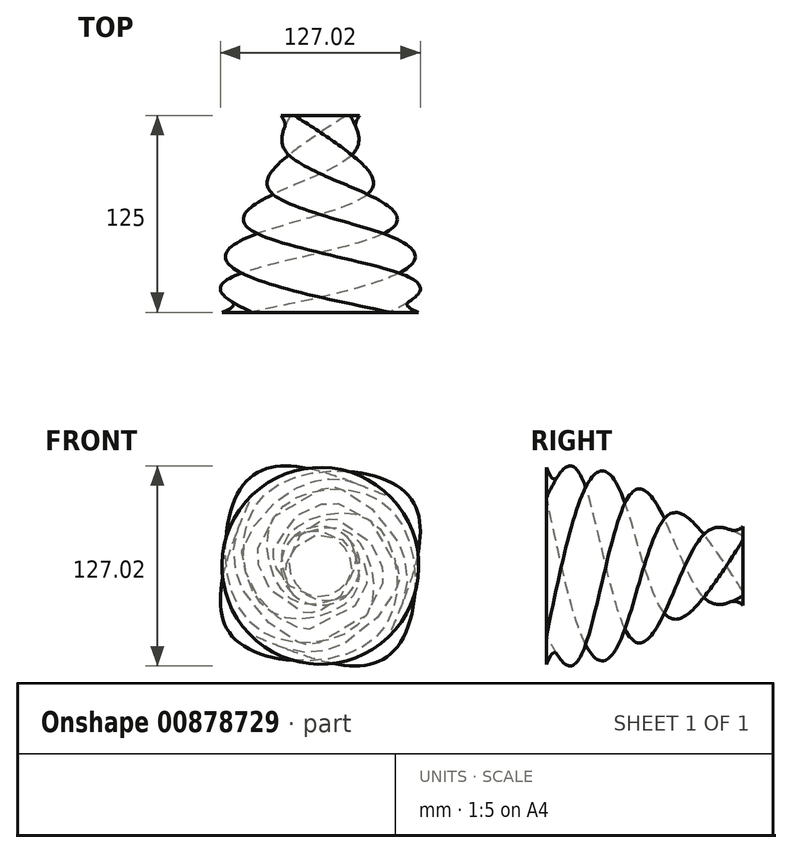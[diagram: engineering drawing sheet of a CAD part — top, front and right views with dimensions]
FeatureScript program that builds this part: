
annotation { "Feature Type Name" : "Feature", "Feature Type Description" : "" }
export const myFeature = defineFeature(function(context is Context, id is Id, definition is map)
    precondition{}
    {
        {
            var Q0;
            Q0=qCreatedBy(makeId("Front.planeOp"),FACE);
            cPlane(context, id + "F0", {"entities" : qUnion([Q0]), "cplaneType" : CPlaneType.OFFSET, "offset" : 25 * mm, "width" : 150 * mm, "height" : 150 * mm});
        }
        {
            var Q0;
            Q0=qCreatedBy(id+"F0.planeOp",FACE);
            cPlane(context, id + "F1", {"entities" : qUnion([Q0]), "cplaneType" : CPlaneType.OFFSET, "offset" : 25 * mm, "width" : 150 * mm, "height" : 150 * mm});
        }
        {
            var Q0;
            Q0=qCreatedBy(id+"F1.planeOp",FACE);
            cPlane(context, id + "F2", {"entities" : qUnion([Q0]), "cplaneType" : CPlaneType.OFFSET, "offset" : 25 * mm, "width" : 150 * mm, "height" : 150 * mm});
        }
        {
            var Q0;
            Q0=qCreatedBy(id+"F2.planeOp",FACE);
            cPlane(context, id + "F3", {"entities" : qUnion([Q0]), "cplaneType" : CPlaneType.OFFSET, "offset" : 25 * mm, "width" : 150 * mm, "height" : 150 * mm});
        }
        {
            var Q0;
            Q0=qCreatedBy(id+"F3.planeOp",FACE);
            cPlane(context, id + "F4", {"entities" : qUnion([Q0]), "cplaneType" : CPlaneType.OFFSET, "offset" : 25 * mm, "width" : 150 * mm, "height" : 150 * mm});
        }
        {
            var Q0;
            Q0=qCreatedBy(makeId("Front.planeOp"),FACE);
            var sketch = newSketch(context, id + "F5", { "sketchPlane" : qUnion([Q0])});
            skCircle(sketch, "E0", {"center": v(0, 0) * mm, "radius": 25 * mm});
            skPoint(sketch, "E1", {"position": v(-16.54, 18.75) * mm});
            skPoint(sketch, "E2", {"position": v(16.54, 18.75) * mm});
            skPoint(sketch, "E3", {"position": v(20.2, -14.74) * mm});
            skPoint(sketch, "E4", {"position": v(-18.95, -16.3) * mm});
            skSolve(sketch);
        }
        {
            var Q0;
            Q0=qCreatedBy(id+"F0.planeOp",FACE);
            var sketch = newSketch(context, id + "F6", { "sketchPlane" : qUnion([Q0])});
            skLineSegment(sketch, "E5.bottom", {"start": v(20, 20) * mm, "end": v(-20, 20) * mm});
            skLineSegment(sketch, "E5.top", {"start": v(20, -20) * mm, "end": v(-20, -20) * mm});
            skLineSegment(sketch, "E5.left", {"start": v(20, 20) * mm, "end": v(20, -20) * mm});
            skLineSegment(sketch, "E5.right", {"start": v(-20, 20) * mm, "end": v(-20, -20) * mm});
            skPoint(sketch, "E5.middle", {"position": v(0, 0) * mm});
            skSolve(sketch);
        }
        {
            var Q0;
            Q0=qCreatedBy(id+"F1.planeOp",FACE);
            var sketch = newSketch(context, id + "F7", { "sketchPlane" : qUnion([Q0])});
            skLineSegment(sketch, "E6.bottom", {"start": v(30, 30) * mm, "end": v(-30, 30) * mm});
            skLineSegment(sketch, "E6.top", {"start": v(30, -30) * mm, "end": v(-30, -30) * mm});
            skLineSegment(sketch, "E6.left", {"start": v(30, 30) * mm, "end": v(30, -30) * mm});
            skLineSegment(sketch, "E6.right", {"start": v(-30, 30) * mm, "end": v(-30, -30) * mm});
            skPoint(sketch, "E6.middle", {"position": v(0, 0) * mm});
            skSolve(sketch);
        }
        {
            var Q0;
            Q0=qCreatedBy(id+"F2.planeOp",FACE);
            var sketch = newSketch(context, id + "F8", { "sketchPlane" : qUnion([Q0])});
            skLineSegment(sketch, "E7.bottom", {"start": v(40, 40) * mm, "end": v(-40, 40) * mm});
            skLineSegment(sketch, "E7.top", {"start": v(40, -40) * mm, "end": v(-40, -40) * mm});
            skLineSegment(sketch, "E7.left", {"start": v(40, 40) * mm, "end": v(40, -40) * mm});
            skLineSegment(sketch, "E7.right", {"start": v(-40, 40) * mm, "end": v(-40, -40) * mm});
            skPoint(sketch, "E7.middle", {"position": v(0, 0) * mm});
            skSolve(sketch);
        }
        {
            var Q0;
            Q0=qCreatedBy(id+"F3.planeOp",FACE);
            var sketch = newSketch(context, id + "F9", { "sketchPlane" : qUnion([Q0])});
            skLineSegment(sketch, "E8.bottom", {"start": v(50, 50) * mm, "end": v(-50, 50) * mm});
            skLineSegment(sketch, "E8.top", {"start": v(50, -50) * mm, "end": v(-50, -50) * mm});
            skLineSegment(sketch, "E8.left", {"start": v(50, 50) * mm, "end": v(50, -50) * mm});
            skLineSegment(sketch, "E8.right", {"start": v(-50, 50) * mm, "end": v(-50, -50) * mm});
            skPoint(sketch, "E8.middle", {"position": v(0, 0) * mm});
            skSolve(sketch);
        }
        {
            var Q0;
            Q0=qCreatedBy(id+"F4.planeOp",FACE);
            var sketch = newSketch(context, id + "F10", { "sketchPlane" : qUnion([Q0])});
            skCircle(sketch, "E9", {"center": v(0, 0) * mm, "radius": 62.5 * mm});
            skPoint(sketch, "E10", {"position": v(-46, -42.3) * mm});
            skPoint(sketch, "E11", {"position": v(-43.26, 45.11) * mm});
            skPoint(sketch, "E12", {"position": v(43.26, 45.11) * mm});
            skPoint(sketch, "E13", {"position": v(44.72, -43.66) * mm});
            skSolve(sketch);
        }
        {
            var Q0;
            Q0=makeQuery(id+"F5.imprint","IMPRINT",FACE,{"disambiguationData":[TD([[makeQuery(id+"F5.imprint","IMPRINT",EDGE,{"derivedFrom":sQuery(id+"F5.wireOp",EDGE,"E0")}),1.0]])]});
            var Q1;
            Q1=makeQuery(id+"F6.imprint","IMPRINT",FACE,{"disambiguationData":[TD([[makeQuery(id+"F6.imprint","IMPRINT",EDGE,{"derivedFrom":sQuery(id+"F6.wireOp",EDGE,"E5.bottom")}),1.0]])]});
            var Q2;
            Q2=makeQuery(id+"F7.imprint","IMPRINT",FACE,{"disambiguationData":[TD([[makeQuery(id+"F7.imprint","IMPRINT",EDGE,{"derivedFrom":sQuery(id+"F7.wireOp",EDGE,"E6.bottom")}),1.0]])]});
            var Q3;
            Q3=makeQuery(id+"F8.imprint","IMPRINT",FACE,{"disambiguationData":[TD([[makeQuery(id+"F8.imprint","IMPRINT",EDGE,{"derivedFrom":sQuery(id+"F8.wireOp",EDGE,"E7.bottom")}),1.0]])]});
            var Q4;
            Q4=makeQuery(id+"F9.imprint","IMPRINT",FACE,{"disambiguationData":[TD([[makeQuery(id+"F9.imprint","IMPRINT",EDGE,{"derivedFrom":sQuery(id+"F9.wireOp",EDGE,"E8.bottom")}),1.0]])]});
            var Q5;
            Q5=makeQuery(id+"F10.imprint","IMPRINT",FACE,{"disambiguationData":[TD([[makeQuery(id+"F10.imprint","IMPRINT",EDGE,{"derivedFrom":sQuery(id+"F10.wireOp",EDGE,"E9")}),1.0]])]});
            var Q6;
            Q6=sQuery(id+"F5.wireOp",VERTEX,"E4");
            var Q7;
            Q7=sQuery(id+"F6.wireOp",VERTEX,"E5.bottom.end");
            var Q8;
            Q8=sQuery(id+"F7.wireOp",VERTEX,"E6.bottom.start");
            var Q9;
            Q9=sQuery(id+"F8.wireOp",VERTEX,"E7.top.start");
            var Q10;
            Q10=sQuery(id+"F9.wireOp",VERTEX,"E8.top.end");
            var Q11;
            Q11=sQuery(id+"F10.wireOp",VERTEX,"E11");
            loft(context, id + "F11", {"sheetProfilesArray" : [{ "sheetProfileEntities" : qUnion([Q0]) }, { "sheetProfileEntities" : qUnion([Q1]) }, { "sheetProfileEntities" : qUnion([Q2]) }, { "sheetProfileEntities" : qUnion([Q3]) }, { "sheetProfileEntities" : qUnion([Q4]) }, { "sheetProfileEntities" : qUnion([Q5]) }], "matchConnections" : true, "connections" : [{ "connectionEntities" : qUnion([Q6, Q7, Q8, Q9, Q10, Q11]), "connectionEdgeQueries" : qUnion([]), "connectionEdgeParameters" : [] }]});
        }
    });
